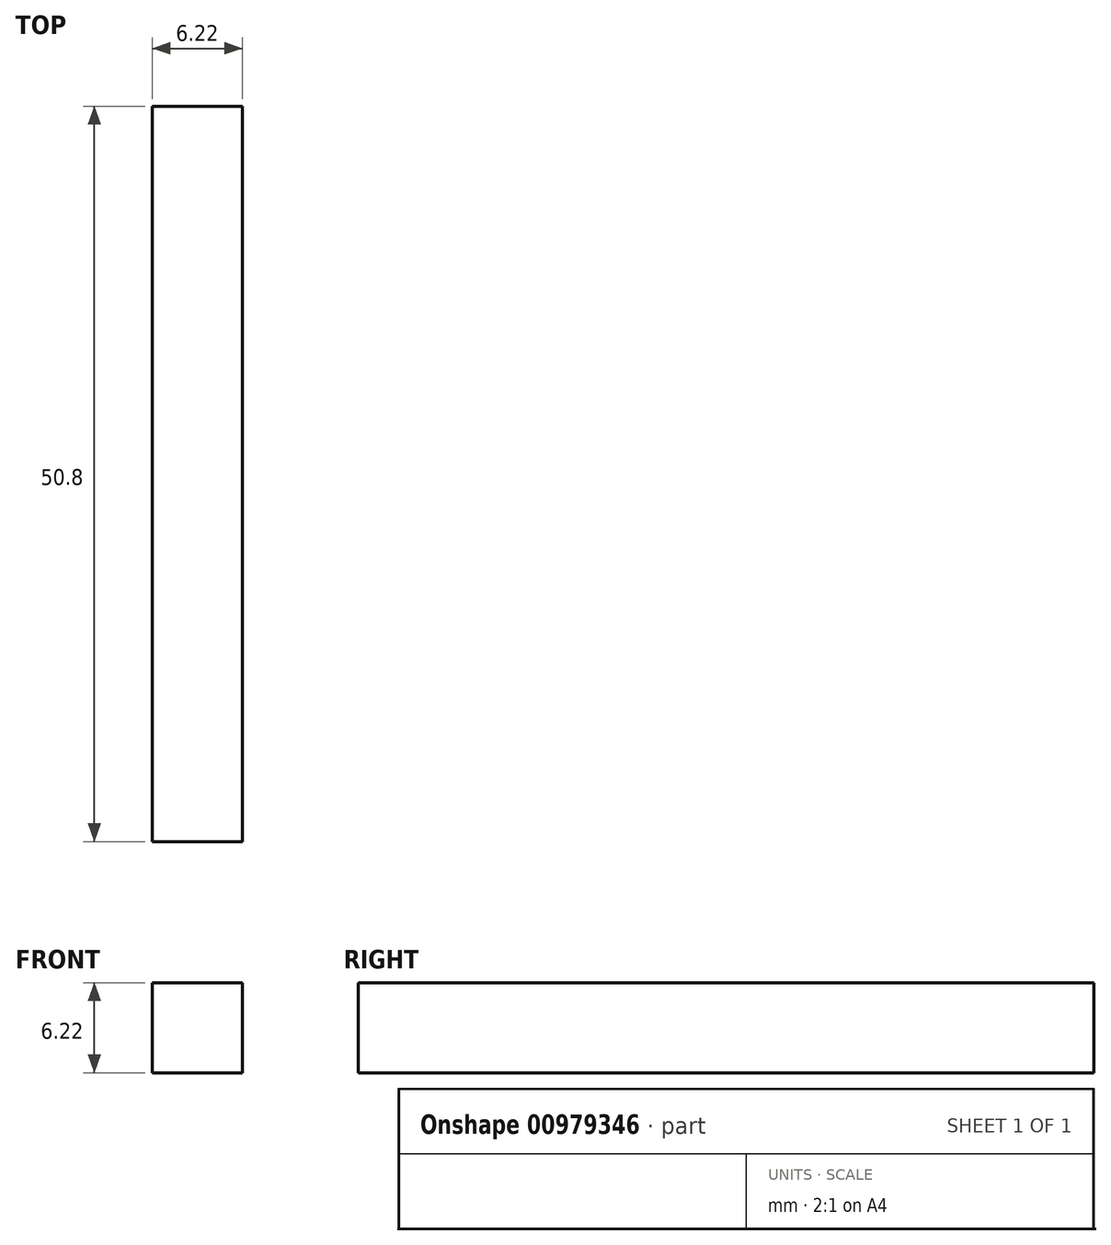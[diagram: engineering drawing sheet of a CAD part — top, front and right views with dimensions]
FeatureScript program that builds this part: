
annotation { "Feature Type Name" : "Feature", "Feature Type Description" : "" }
export const myFeature = defineFeature(function(context is Context, id is Id, definition is map)
    precondition{}
    {
        {
            var Q0;
            Q0=qCreatedBy(makeId("Top.planeOp"),FACE);
            var sketch = newSketch(context, id + "F0", { "sketchPlane" : qUnion([Q0])});
            skLineSegment(sketch, "E0.bottom", {"start": v(0, 0) * mm, "end": v(6.22, 0) * mm});
            skLineSegment(sketch, "E0.top", {"start": v(0, 50.8) * mm, "end": v(6.22, 50.8) * mm});
            skLineSegment(sketch, "E0.left", {"start": v(0, 0) * mm, "end": v(0, 50.8) * mm});
            skLineSegment(sketch, "E0.right", {"start": v(6.22, 0) * mm, "end": v(6.22, 50.8) * mm});
            skSolve(sketch);
        }
        {
            var Q0;
            Q0=makeQuery(id+"F0.imprint","IMPRINT",FACE,{"disambiguationData":[TD([[makeQuery(id+"F0.imprint","IMPRINT",EDGE,{"derivedFrom":sQuery(id+"F0.wireOp",EDGE,"E0.bottom")}),1.0]])]});
            extrude(context, id + "F1", {"entities" : qUnion([Q0]), "depth" : 6.22 * mm, "offsetDistance" : 25.4 * mm});
        }
    });
